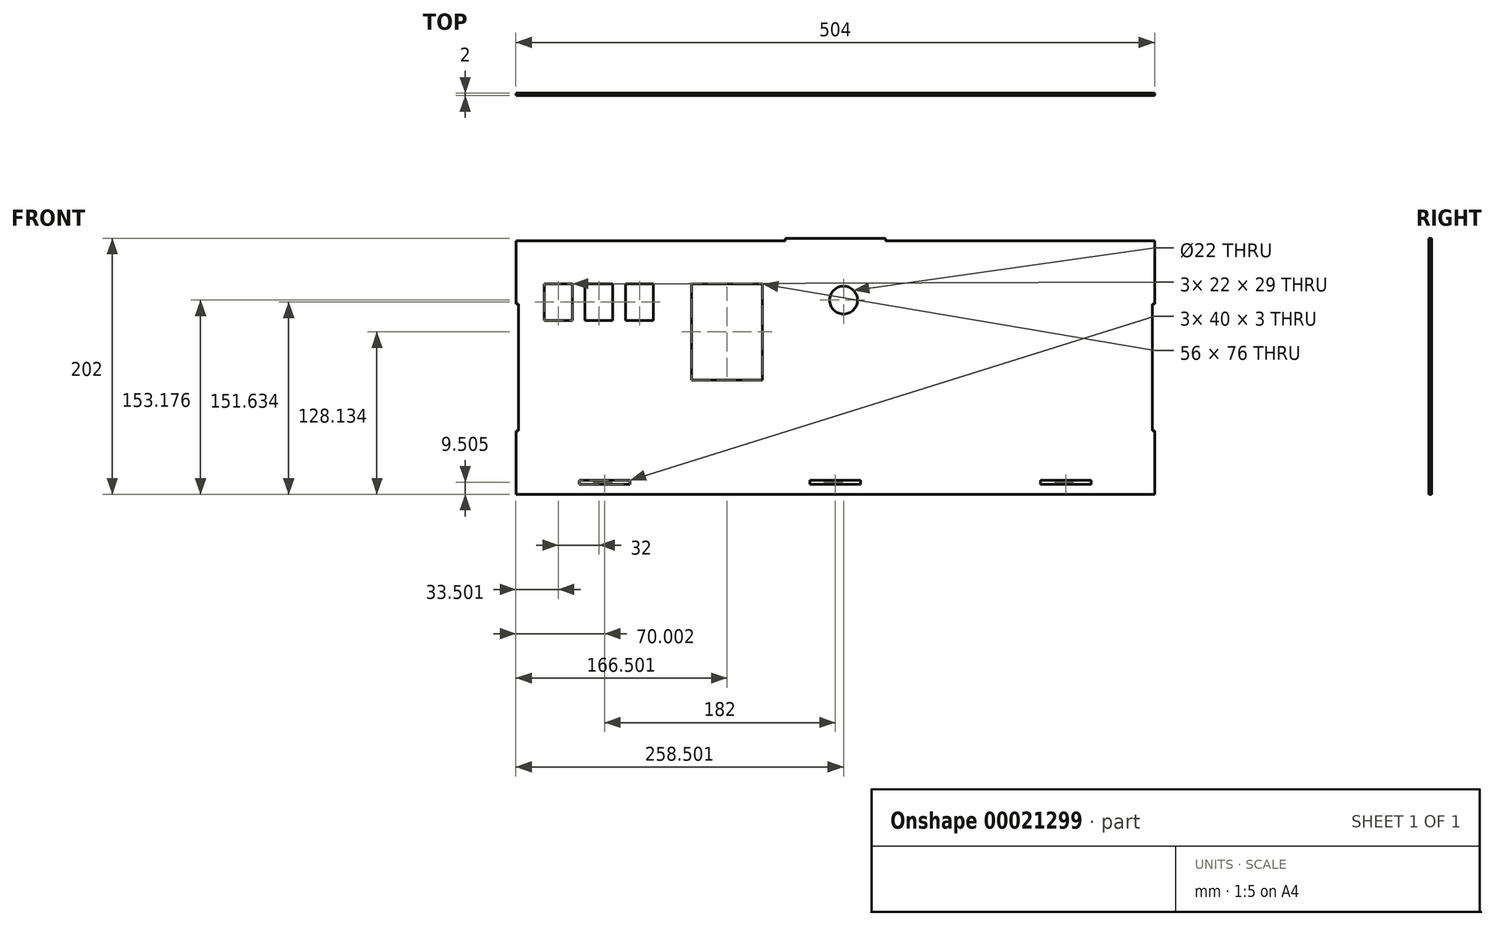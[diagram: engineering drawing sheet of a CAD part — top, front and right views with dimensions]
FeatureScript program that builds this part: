
annotation { "Feature Type Name" : "Feature", "Feature Type Description" : "" }
export const myFeature = defineFeature(function(context is Context, id is Id, definition is map)
    precondition{}
    {
        {
            var Q0;
            Q0=qCreatedBy(makeId("Front.planeOp"),FACE);
            var sketch = newSketch(context, id + "F0", { "sketchPlane" : qUnion([Q0])});
            skLineSegment(sketch, "E0.bottom", {"start": v(-246.74, 62.28) * mm, "end": v(257.26, 62.28) * mm});
            skLineSegment(sketch, "E0.top", {"start": v(-246.74, -137.72) * mm, "end": v(257.26, -137.72) * mm});
            skLineSegment(sketch, "E0.left", {"start": v(-246.74, 62.28) * mm, "end": v(-246.74, -137.72) * mm});
            skLineSegment(sketch, "E0.right", {"start": v(257.26, 62.28) * mm, "end": v(257.26, -137.72) * mm});
            skSolve(sketch);
        }
        {
            var Q0;
            Q0 = qSketchRegion(id + "F0", true);
            extrude(context, id + "F1", {"entities" : qUnion([Q0]), "depth" : 2 * mm});
        }
        {
            var Q0;
            Q0=makeQuery(id+"F1.opExtrude","CAP_FACE",FACE,{"disambiguationData":[OSD([sQuery(id+"F0.wireOp",EDGE,"E0.bottom"),sQuery(id+"F0.wireOp",EDGE,"E0.top"),sQuery(id+"F0.wireOp",EDGE,"E0.left"),sQuery(id+"F0.wireOp",EDGE,"E0.right")])],"isStart":false});
            var sketch = newSketch(context, id + "F2", { "sketchPlane" : qUnion([Q0])});
            skCircle(sketch, "E1", {"center": v(11.76, 15.46) * mm, "radius": 11 * mm});
            skLineSegment(sketch, "E2.bottom", {"start": v(-108.24, 28.41) * mm, "end": v(-52.24, 28.41) * mm});
            skLineSegment(sketch, "E2.top", {"start": v(-108.24, -47.59) * mm, "end": v(-52.24, -47.59) * mm});
            skLineSegment(sketch, "E2.left", {"start": v(-108.24, 28.41) * mm, "end": v(-108.24, -47.59) * mm});
            skLineSegment(sketch, "E2.right", {"start": v(-52.24, 28.41) * mm, "end": v(-52.24, -47.59) * mm});
            skLineSegment(sketch, "E3.bottom", {"start": v(-192.24, 28.41) * mm, "end": v(-170.24, 28.41) * mm});
            skLineSegment(sketch, "E3.top", {"start": v(-192.24, -0.59) * mm, "end": v(-170.24, -0.59) * mm});
            skLineSegment(sketch, "E3.left", {"start": v(-192.24, 28.41) * mm, "end": v(-192.24, -0.59) * mm});
            skLineSegment(sketch, "E3.right", {"start": v(-170.24, 28.41) * mm, "end": v(-170.24, -0.59) * mm});
            skLineSegment(sketch, "E4.bottom", {"start": v(-160.24, 28.41) * mm, "end": v(-138.24, 28.41) * mm});
            skLineSegment(sketch, "E4.top", {"start": v(-160.24, -0.59) * mm, "end": v(-138.24, -0.59) * mm});
            skLineSegment(sketch, "E4.left", {"start": v(-160.24, 28.41) * mm, "end": v(-160.24, -0.59) * mm});
            skLineSegment(sketch, "E4.right", {"start": v(-138.24, 28.41) * mm, "end": v(-138.24, -0.59) * mm});
            skLineSegment(sketch, "E5.bottom", {"start": v(-224.24, 28.41) * mm, "end": v(-202.24, 28.41) * mm});
            skLineSegment(sketch, "E5.top", {"start": v(-224.24, -0.59) * mm, "end": v(-202.24, -0.59) * mm});
            skLineSegment(sketch, "E5.left", {"start": v(-224.24, 28.41) * mm, "end": v(-224.24, -0.59) * mm});
            skLineSegment(sketch, "E5.right", {"start": v(-202.24, 28.41) * mm, "end": v(-202.24, -0.59) * mm});
            skSolve(sketch);
        }
        {
            var Q0;
            Q0 = qSketchRegion(id + "F2", true);
            extrude(context, id + "F3", {"entities" : qUnion([Q0]), "operationType" : NewBodyOperationType.REMOVE, "oppositeDirection" : true, "depth" : 25 * mm});
        }
        {
            var Q0;
            Q0=makeQuery(id+"F1.opExtrude","CAP_FACE",FACE,{"disambiguationData":[OSD([sQuery(id+"F0.wireOp",EDGE,"E0.bottom"),sQuery(id+"F0.wireOp",EDGE,"E0.top"),sQuery(id+"F0.wireOp",EDGE,"E0.left"),sQuery(id+"F0.wireOp",EDGE,"E0.right")])],"isStart":false});
            var sketch = newSketch(context, id + "F4", { "sketchPlane" : qUnion([Q0])});
            skLineSegment(sketch, "E6.bottom", {"start": v(-196.74, -126.72) * mm, "end": v(-156.74, -126.72) * mm});
            skLineSegment(sketch, "E6.top", {"start": v(-196.74, -129.72) * mm, "end": v(-156.74, -129.72) * mm});
            skLineSegment(sketch, "E6.left", {"start": v(-196.74, -126.72) * mm, "end": v(-196.74, -129.72) * mm});
            skLineSegment(sketch, "E6.right", {"start": v(-156.74, -126.72) * mm, "end": v(-156.74, -129.72) * mm});
            skLineSegment(sketch, "E7.bottom", {"start": v(-14.74, -126.72) * mm, "end": v(25.26, -126.72) * mm});
            skLineSegment(sketch, "E7.top", {"start": v(-14.74, -129.72) * mm, "end": v(25.26, -129.72) * mm});
            skLineSegment(sketch, "E7.left", {"start": v(-14.74, -126.72) * mm, "end": v(-14.74, -129.72) * mm});
            skLineSegment(sketch, "E7.right", {"start": v(25.26, -126.72) * mm, "end": v(25.26, -129.72) * mm});
            skLineSegment(sketch, "E8.bottom", {"start": v(167.26, -126.72) * mm, "end": v(207.26, -126.72) * mm});
            skLineSegment(sketch, "E8.top", {"start": v(167.26, -129.72) * mm, "end": v(207.26, -129.72) * mm});
            skLineSegment(sketch, "E8.left", {"start": v(167.26, -126.72) * mm, "end": v(167.26, -129.72) * mm});
            skLineSegment(sketch, "E8.right", {"start": v(207.26, -126.72) * mm, "end": v(207.26, -129.72) * mm});
            skLineSegment(sketch, "E9", {"start": v(5.26, 62.28) * mm, "end": v(5.26, -137.72) * mm, "construction": true});
            skSolve(sketch);
        }
        {
            var Q0;
            Q0 = qSketchRegion(id + "F4", true);
            extrude(context, id + "F5", {"entities" : qUnion([Q0]), "operationType" : NewBodyOperationType.REMOVE, "oppositeDirection" : true, "depth" : 25 * mm});
        }
        {
            var Q0;
            Q0=makeQuery(id+"F1.opExtrude","CAP_FACE",FACE,{"disambiguationData":[OSD([sQuery(id+"F0.wireOp",EDGE,"E0.bottom"),sQuery(id+"F0.wireOp",EDGE,"E0.top"),sQuery(id+"F0.wireOp",EDGE,"E0.left"),sQuery(id+"F0.wireOp",EDGE,"E0.right")])],"isStart":false});
            var sketch = newSketch(context, id + "F6", { "sketchPlane" : qUnion([Q0])});
            skLineSegment(sketch, "E10.bottom", {"start": v(-246.74, 12.28) * mm, "end": v(-244.74, 12.28) * mm});
            skLineSegment(sketch, "E10.top", {"start": v(-246.74, -87.72) * mm, "end": v(-244.74, -87.72) * mm});
            skLineSegment(sketch, "E10.left", {"start": v(-246.74, 12.28) * mm, "end": v(-246.74, -87.72) * mm});
            skLineSegment(sketch, "E10.right", {"start": v(-244.74, 12.28) * mm, "end": v(-244.74, -87.72) * mm});
            skLineSegment(sketch, "E11.bottom", {"start": v(257.26, 12.28) * mm, "end": v(255.26, 12.28) * mm});
            skLineSegment(sketch, "E11.top", {"start": v(257.26, -87.72) * mm, "end": v(255.26, -87.72) * mm});
            skLineSegment(sketch, "E11.left", {"start": v(257.26, 12.28) * mm, "end": v(257.26, -87.72) * mm});
            skLineSegment(sketch, "E11.right", {"start": v(255.26, 12.28) * mm, "end": v(255.26, -87.72) * mm});
            skSolve(sketch);
        }
        {
            var Q0;
            Q0 = qSketchRegion(id + "F6", true);
            extrude(context, id + "F7", {"entities" : qUnion([Q0]), "operationType" : NewBodyOperationType.REMOVE, "oppositeDirection" : true, "depth" : 25 * mm});
        }
        {
            var Q0;
            Q0=makeQuery(id+"F1.opExtrude","CAP_FACE",FACE,{"disambiguationData":[OSD([sQuery(id+"F0.wireOp",EDGE,"E0.bottom"),sQuery(id+"F0.wireOp",EDGE,"E0.top"),sQuery(id+"F0.wireOp",EDGE,"E0.left"),sQuery(id+"F0.wireOp",EDGE,"E0.right")])],"isStart":false});
            var sketch = newSketch(context, id + "F8", { "sketchPlane" : qUnion([Q0])});
            skLineSegment(sketch, "E12.rect.bottom", {"start": v(44.76, 64.28) * mm, "end": v(-34.24, 64.28) * mm});
            skLineSegment(sketch, "E12.rect.top", {"start": v(44.76, 60.28) * mm, "end": v(-34.24, 60.28) * mm});
            skLineSegment(sketch, "E12.rect.left", {"start": v(44.76, 64.28) * mm, "end": v(44.76, 60.28) * mm});
            skLineSegment(sketch, "E12.rect.right", {"start": v(-34.24, 64.28) * mm, "end": v(-34.24, 60.28) * mm});
            skPoint(sketch, "E12.rect.middle", {"position": v(5.26, 62.28) * mm});
            skSolve(sketch);
        }
        {
            var Q0;
            Q0 = qSketchRegion(id + "F8", true);
            extrude(context, id + "F9", {"entities" : qUnion([Q0]), "operationType" : NewBodyOperationType.ADD, "oppositeDirection" : true, "depth" : 2 * mm});
        }
    });
